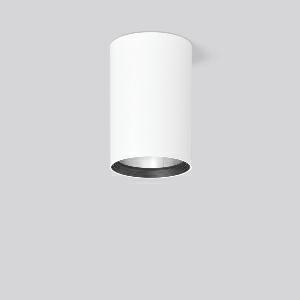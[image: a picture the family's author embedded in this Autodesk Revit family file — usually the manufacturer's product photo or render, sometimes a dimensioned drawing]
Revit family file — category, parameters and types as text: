
# Revit family: heledon_maxi_a_931226_002_3_f45d
name_source: partatom
category: Lighting Fixtures
units: mm (PartAtom-declared; Revit-internal decimal feet)

## family parameters
Cut with Voids When Loaded = No
Host = Face
Light Source = No
Part Type = Normal
Room Calculation Point = No
Round Connector Dimension = Use Diameter
Shared = No

## types (1)
- HELEDON maxi A (1 x LED Modul 935, 4200 lm, 3500)
    Apparent Load = 35 VA
    Approval mark = CE
    CIE Flux Codes = 97 100 100 100 100
    Color Rendering = 92
    Color Temperature = 3500
    Default Elevation = 1800 mm
    Description = Series: HELEDON maxi
Cylindrical surface-mounted downlight. Housing: die-cast aluminium, powder-coated. Internal ceiling frame polycarbonate with bayonet mounting. Black plastic ring and recessed LED to prevent glare from the side. Optical assembly with reflector made of MIRO-Silver with 98% total light reflection for outstanding efficiency - can be changed without tools. Best colour rendering index Ra>90. Suitable for Ceiling mounting. Easy installation with a separate ceiling frame with bayonet mounting and plug connection. Driver integrated. Connected via plug-in connector. High quality converter without flickering and stroboscopic effect. The following accessories can be mounted without use of tools: interchangeable lenses, decorative glasses, honeycomb louvre, clear and frosted diffusers, white interchangeable plastic ring. 
Colour: traffic white, matt (RAL 9016)
Diameter: 123 mm
Height: 183 mm
Lamp: LED
Socket: without socket
Colour temperature: 3500K
Colour rendering index (CRI): 92
System power: 35 W
Rated luminous flux: 4200 lm
Luminous efficiency: 120 lm/W
Control gear: Regulated power supply
Protection class: I
Type of protection: IP 20
    Height = 183 mm
    Lamp = 1 x LED Modul 935
    Lamp Light Flux = 4200 lm
    Lamp count = 1
    Length = 123 mm
    Lifetime = 50000 h
    Luminous efficacy = 120 lm/W
    Manufacturer = RZB
    ModVariant = No
    Model = 931226.002.3
    Mounting Place = Ceiling
    Mounting Type = Surface mounted
    Number of Poles = 1
    OnlyDefault = Yes
    Power Factor = 1
    Product Name = HELEDON maxi A
    Product group = Surface mounted downlights
    ProductGroupID = 302
    Protection Class = Protection class I
    Protection Degree = IP 20
    RLX_Detail_Level = 1
    RLX_Emergency_Light_Flux = 0 lm
    RLX_Emergency_Type = 0
    RLX_Emergency_Type_DB = No
    RlxData = <blob elided: 96865 chars, md5=a8476fd0>
    Socket = socket
    Standby Power = 0 W
    System Light Flux = 4200 lm
    System Power = 35 W
    Type Comments = Product without accessories
    Type Image = 931192.002.jpg
    URL = http://relux.com
    VarID = ---
    Voltage = 230 V
    Voltage Range = 220-240 V
    Weight = 0.00 kg
    Width = 0 mm  [stored 0 ft]

note: [stored X ft] marks values corroborated as IEEE doubles in the binary element streams (Revit-internal decimal feet)

## geometry (parser evidence)
native form markers: Blend x4, Sweep x12
no freeform markers — native parametric forms only
